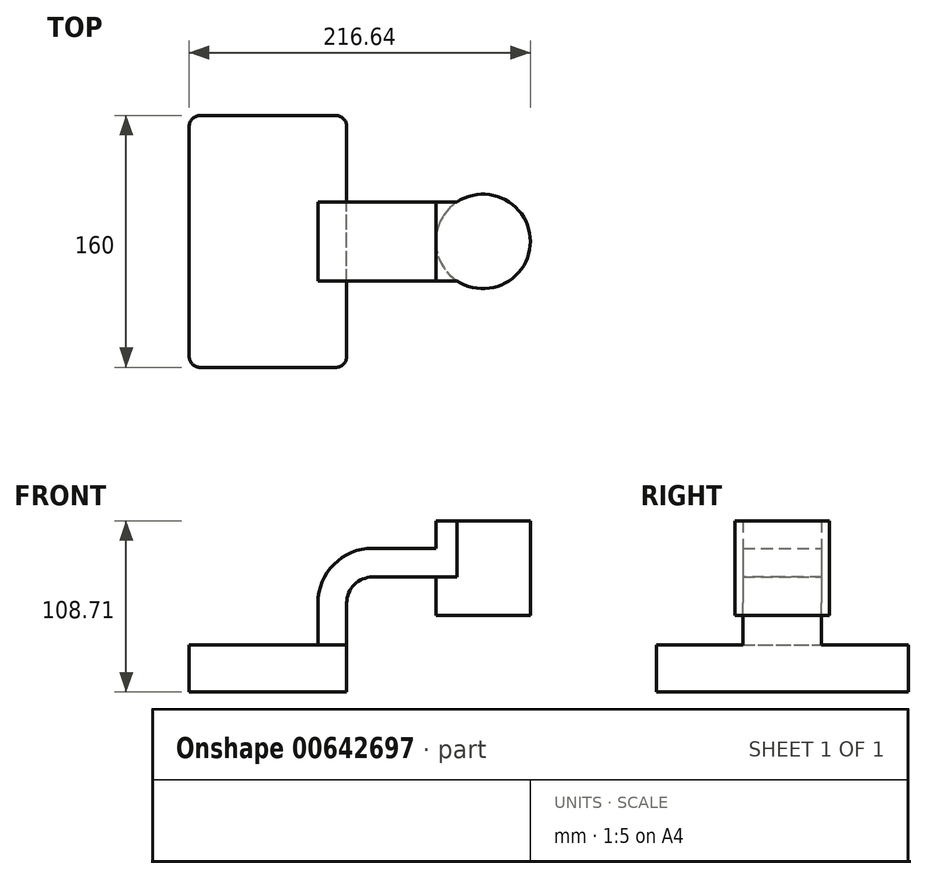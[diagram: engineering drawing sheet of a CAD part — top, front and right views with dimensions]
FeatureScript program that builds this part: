
annotation { "Feature Type Name" : "Feature", "Feature Type Description" : "" }
export const myFeature = defineFeature(function(context is Context, id is Id, definition is map)
    precondition{}
    {
        {
            var Q0;
            Q0=qCreatedBy(makeId("Front.planeOp"),FACE);
            var sketch = newSketch(context, id + "F0", { "sketchPlane" : qUnion([Q0])});
            skLineSegment(sketch, "E0.bottom", {"start": v(-50, 15) * mm, "end": v(50, 15) * mm});
            skLineSegment(sketch, "E0.top", {"start": v(-50, -15) * mm, "end": v(50, -15) * mm});
            skLineSegment(sketch, "E0.left", {"start": v(-50, 15) * mm, "end": v(-50, -15) * mm});
            skLineSegment(sketch, "E0.right", {"start": v(50, 15) * mm, "end": v(50, -15) * mm});
            skPoint(sketch, "E0.middle", {"position": v(0, 0) * mm});
            skLineSegment(sketch, "E1.bottom", {"start": v(106.64, 93.7) * mm, "end": v(166.64, 93.7) * mm});
            skLineSegment(sketch, "E1.top", {"start": v(106.64, 33.7) * mm, "end": v(166.64, 33.7) * mm});
            skLineSegment(sketch, "E1.left", {"start": v(106.64, 93.7) * mm, "end": v(106.64, 33.7) * mm});
            skLineSegment(sketch, "E1.right", {"start": v(166.64, 93.7) * mm, "end": v(166.64, 33.7) * mm});
            skPoint(sketch, "E1.middle", {"position": v(136.64, 63.7) * mm});
            skLineSegment(sketch, "E2", {"start": v(50, 15) * mm, "end": v(50, 41.47) * mm});
            skArc(sketch, "E3", {"start": v(50, 41.47) * mm, "mid": v(54.85, 53.19) * mm, "end": v(66.56, 58.04) * mm});
            skLineSegment(sketch, "E4", {"start": v(66.56, 58.04) * mm, "end": v(136.64, 58.04) * mm});
            skLineSegment(sketch, "E5.0", {"start": v(66.56, 76.35) * mm, "end": v(135.96, 76.35) * mm});
            skArc(sketch, "E5.1", {"start": v(31.69, 41.47) * mm, "mid": v(41.9, 66.14) * mm, "end": v(66.56, 76.35) * mm});
            skLineSegment(sketch, "E5.2", {"start": v(31.69, 15) * mm, "end": v(31.69, 41.47) * mm});
            skFitSpline(sketch, "E6", {"points": [v(-50, 15) * mm, v(66.56, 76.35) * mm], "startDerivative": vector(0, 120.2) * mm, "endDerivative": vector(143.54, 0) * mm});
            skLineSegment(sketch, "E7", {"start": v(136.64, 63.7) * mm, "end": v(136.64, 93.7) * mm});
            skLineSegment(sketch, "E8", {"start": v(136.64, 63.7) * mm, "end": v(136.64, 33.7) * mm});
            skSolve(sketch);
        }
        {
            var Q0;
            Q0=makeQuery(id+"F0.imprint","IMPRINT",FACE,{"disambiguationData":[TD([[makeQuery(id+"F0.imprint","IMPRINT",EDGE,{"derivedFrom":sQuery(id+"F0.wireOp",EDGE,"E0.top")}),1.0]])]});
            extrude(context, id + "F1", {"entities" : qUnion([Q0]), "endBound" : BoundingType.SYMMETRIC, "depth" : 160 * mm, "offsetDistance" : 25 * mm});
        }
        {
            var Q0;
            {var subQ1=sQuery(id+"F0.wireOp",EDGE,"E2");Q0=makeQuery(id+"F0.imprint","IMPRINT",FACE,{"disambiguationData":[TD([[makeQuery(id+"F0.imprint","IMPRINT",EDGE,{"derivedFrom":subQ1}),1.0]])]});}
            extrude(context, id + "F2", {"entities" : qUnion([Q0]), "operationType" : NewBodyOperationType.ADD, "endBound" : BoundingType.SYMMETRIC, "depth" : 50 * mm, "offsetDistance" : 25 * mm});
        }
        {
            var Q0;
            Q0=makeQuery(id+"F0.imprint","IMPRINT",FACE,{"disambiguationData":[TD([[makeQuery(id+"F0.imprint","IMPRINT",EDGE,{"derivedFrom":sQuery(id+"F0.wireOp",EDGE,"E5.1")}),1.0]])]});
            extrude(context, id + "F3", {"entities" : qUnion([Q0]), "operationType" : NewBodyOperationType.ADD, "endBound" : BoundingType.SYMMETRIC, "depth" : 10 * mm, "offsetDistance" : 25 * mm});
        }
        {
            var Q0;
            {var subQ1=sQuery(id+"F0.wireOp",EDGE,"E5.0");var subQ5=sQuery(id+"F0.wireOp",EDGE,"E1.left");var subQ6=makeQuery(id+"F0.imprint","INTERSECT",VERTEX,{"derivedFrom":[subQ5,subQ1]});Q0=makeQuery(id+"F0.imprint","IMPRINT",FACE,{"disambiguationData":[TD([[makeQuery(id+"F0.imprint","IMPRINT",EDGE,{"disambiguationData":[TD([[subQ6,-1.0]])],"derivedFrom":subQ5}),1.0]])]});}
            extrude(context, id + "F4", {"entities" : qUnion([Q0]), "operationType" : NewBodyOperationType.ADD, "endBound" : BoundingType.SYMMETRIC, "depth" : 50 * mm, "offsetDistance" : 25 * mm});
        }
        {
            var Q0;
            {var subQ4=sQuery(id+"F0.wireOp",EDGE,"E1.right");Q0=makeQuery(id+"F0.imprint","IMPRINT",FACE,{"disambiguationData":[TD([[makeQuery(id+"F0.imprint","IMPRINT",EDGE,{"derivedFrom":subQ4}),-1.0]])]});}
            var Q1;
            Q1=sQuery(id+"F0.wireOp",EDGE,"E7");
            revolve(context, id + "F5", {"operationType" : NewBodyOperationType.ADD, "entities" : qUnion([Q0]), "axis" : qUnion([Q1]), "revolveType" : RevolveType.FULL});
        }
        {
            var Q0;
            Q0=makeQuery(id+"F1.opExtrude","CAP_EDGE",EDGE,{"disambiguationData":[OSD([sQuery(id+"F0.wireOp",EDGE,"E0.right")])],"isStart":false});
            var Q1;
            Q1=makeQuery(id+"F1.opExtrude","CAP_EDGE",EDGE,{"disambiguationData":[OSD([sQuery(id+"F0.wireOp",EDGE,"E0.left")])],"isStart":false});
            var Q2;
            Q2=makeQuery(id+"F1.opExtrude","CAP_EDGE",EDGE,{"disambiguationData":[OSD([sQuery(id+"F0.wireOp",EDGE,"E0.right")])],"isStart":true});
            var Q3;
            Q3=makeQuery(id+"F1.opExtrude","CAP_EDGE",EDGE,{"disambiguationData":[OSD([sQuery(id+"F0.wireOp",EDGE,"E0.left")])],"isStart":true});
            fillet(context, id + "F6", {"entities" : qUnion([Q0, Q1, Q2, Q3]), "radius" : 7 * mm, "tangentPropagation" : true, "allowEdgeOverflow" : false});
        }
    });
